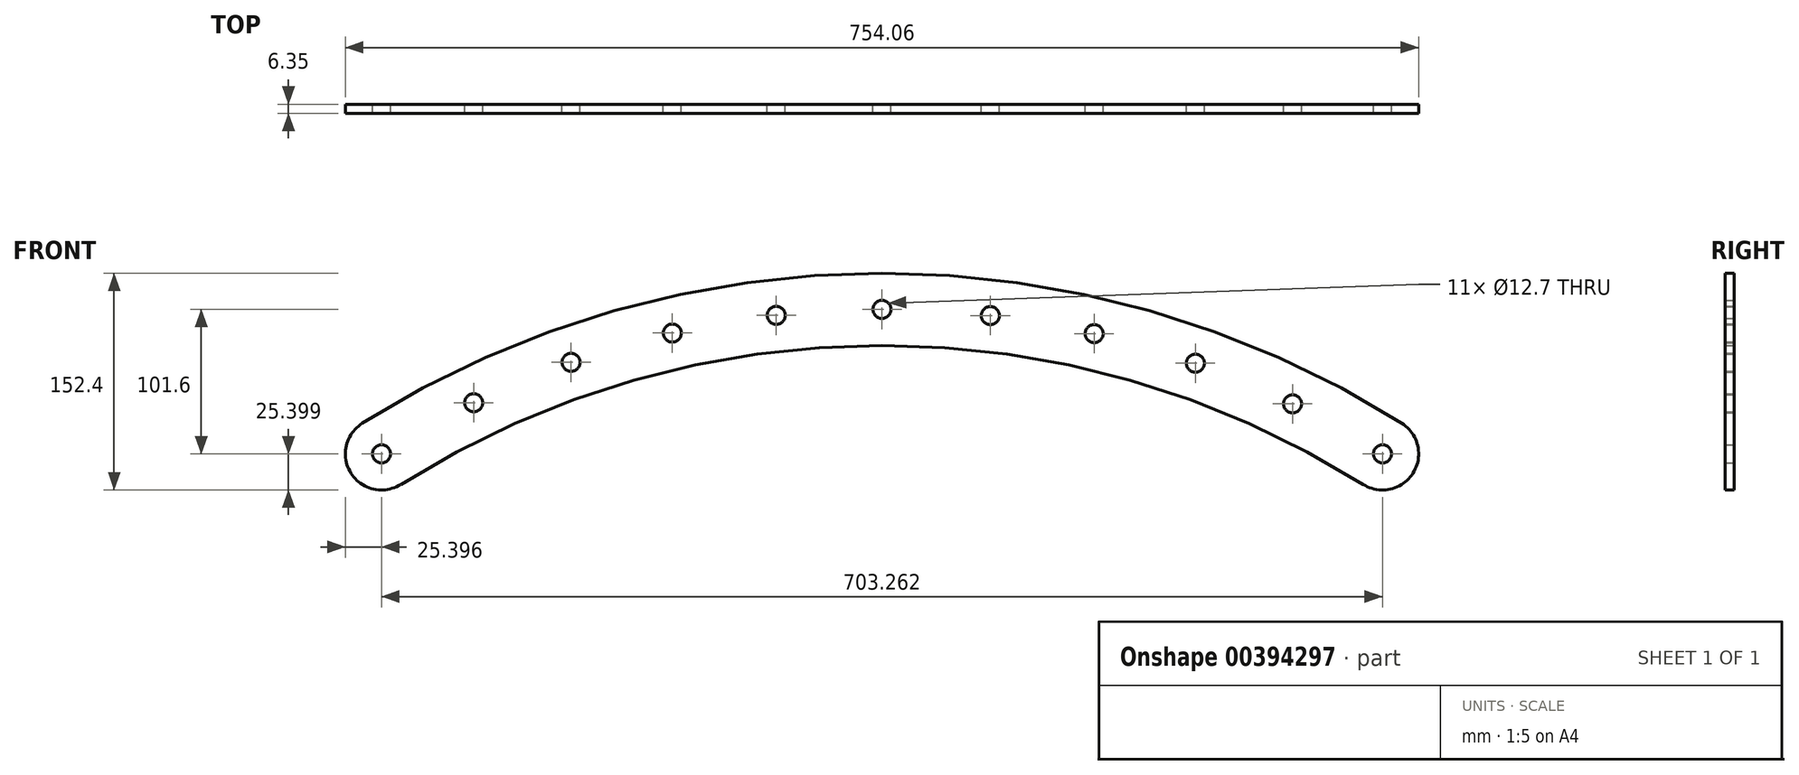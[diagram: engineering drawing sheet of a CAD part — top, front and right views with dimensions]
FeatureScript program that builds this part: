
annotation { "Feature Type Name" : "Feature", "Feature Type Description" : "" }
export const myFeature = defineFeature(function(context is Context, id is Id, definition is map)
    precondition{}
    {
        {
            var Q0;
            Q0=qCreatedBy(makeId("Front.planeOp"),FACE);
            var sketch = newSketch(context, id + "F0", { "sketchPlane" : qUnion([Q0])});
            skCircle(sketch, "E0", {"center": v(-115.64, -12.6) * mm, "radius": 6.35 * mm});
            skCircle(sketch, "E1", {"center": v(587.62, -12.6) * mm, "radius": 6.35 * mm});
            skCircle(sketch, "E2", {"center": v(235.99, 89) * mm, "radius": 6.35 * mm});
            skArc(sketch, "E3.0", {"start": v(601.17, 8.88) * mm, "mid": v(235.99, 114.4) * mm, "end": v(-129.2, 8.88) * mm});
            skArc(sketch, "E4.0", {"start": v(574.07, -34.09) * mm, "mid": v(235.99, 63.6) * mm, "end": v(-102.1, -34.09) * mm});
            skCircle(sketch, "E5", {"center": v(-50.87, 23.32) * mm, "radius": 6.35 * mm});
            skCircle(sketch, "E6", {"center": v(17.52, 51.75) * mm, "radius": 6.35 * mm});
            skCircle(sketch, "E7", {"center": v(88.67, 72.33) * mm, "radius": 6.35 * mm});
            skCircle(sketch, "E8", {"center": v(161.67, 84.8) * mm, "radius": 6.35 * mm});
            skCircle(sketch, "E9", {"center": v(312.09, 84.6) * mm, "radius": 6.35 * mm});
            skCircle(sketch, "E10", {"center": v(385.06, 71.92) * mm, "radius": 6.35 * mm});
            skCircle(sketch, "E11", {"center": v(456.15, 51.15) * mm, "radius": 6.35 * mm});
            skCircle(sketch, "E12", {"center": v(524.46, 22.54) * mm, "radius": 6.35 * mm});
            skArc(sketch, "E13", {"start": v(601.17, 8.88) * mm, "mid": v(609.1, -26.15) * mm, "end": v(574.07, -34.09) * mm});
            skArc(sketch, "E14", {"start": v(-129.2, 8.88) * mm, "mid": v(-137.13, -26.15) * mm, "end": v(-102.1, -34.09) * mm});
            skSolve(sketch);
        }
        {
            var Q0;
            Q0=makeQuery(id+"F0.imprint","IMPRINT",FACE,{"disambiguationData":[TD([[makeQuery(id+"F0.imprint","IMPRINT",EDGE,{"derivedFrom":sQuery(id+"F0.wireOp",EDGE,"E0")}),-1.0]])]});
            extrude(context, id + "F1", {"entities" : qUnion([Q0]), "depth" : 6.35 * mm});
        }
    });
